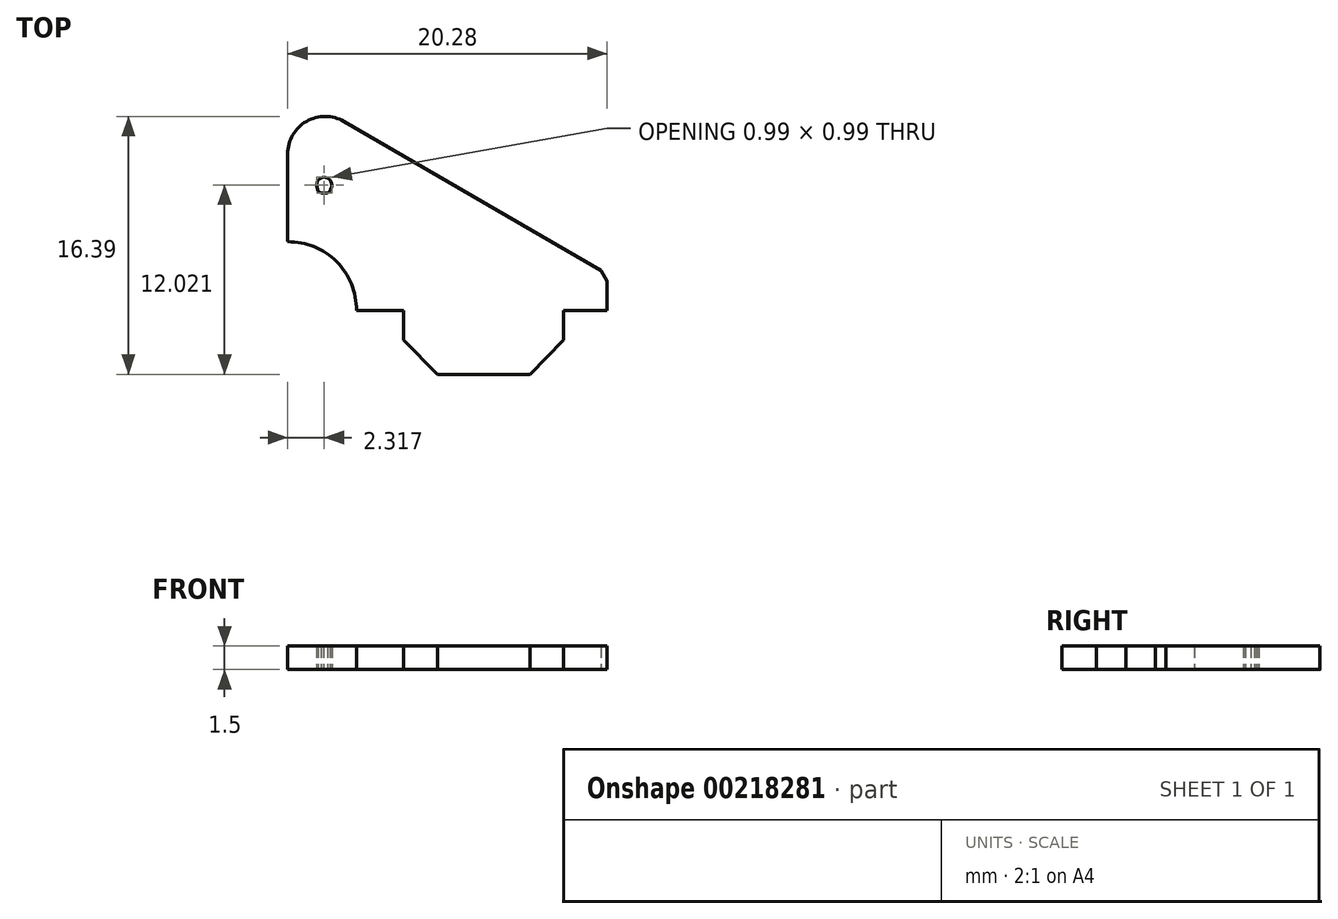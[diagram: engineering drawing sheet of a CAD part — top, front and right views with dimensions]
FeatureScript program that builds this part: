
annotation { "Feature Type Name" : "Feature", "Feature Type Description" : "" }
export const myFeature = defineFeature(function(context is Context, id is Id, definition is map)
    precondition{}
    {
        {
            var Q0;
            Q0=qCreatedBy(makeId("Top.planeOp"),FACE);
            var sketch = newSketch(context, id + "F0", { "sketchPlane" : qUnion([Q0])});
            skLineSegment(sketch, "E0", {"start": v(-0.76, -7.26) * mm, "end": v(5.12, -7.26) * mm});
            skLineSegment(sketch, "E1", {"start": v(5.12, -7.26) * mm, "end": v(7.23, -5.1) * mm});
            skLineSegment(sketch, "E2", {"start": v(7.23, -5.1) * mm, "end": v(7.23, -3.2) * mm});
            skLineSegment(sketch, "E3", {"start": v(7.23, -3.2) * mm, "end": v(10, -3.2) * mm});
            skLineSegment(sketch, "E4", {"start": v(10, -3.2) * mm, "end": v(10, -1.35) * mm});
            skLineSegment(sketch, "E5", {"start": v(-10.28, 1.16) * mm, "end": v(-10.28, 6.74) * mm});
            skLineSegment(sketch, "E6", {"start": v(-0.76, -7.26) * mm, "end": v(-2.94, -5.1) * mm});
            skLineSegment(sketch, "E7", {"start": v(-2.94, -5.1) * mm, "end": v(-2.94, -3.2) * mm});
            skLineSegment(sketch, "E8", {"start": v(-2.94, -3.2) * mm, "end": v(-5.92, -3.2) * mm});
            skLineSegment(sketch, "E9", {"start": v(-7.75, 4.26) * mm, "end": v(-7.58, 4.38) * mm});
            skLineSegment(sketch, "E10", {"start": v(-7.58, 4.38) * mm, "end": v(-7.47, 4.73) * mm});
            skLineSegment(sketch, "E11", {"start": v(-7.47, 4.73) * mm, "end": v(-7.52, 4.96) * mm});
            skLineSegment(sketch, "E12", {"start": v(-7.52, 4.96) * mm, "end": v(-7.58, 5.09) * mm});
            skLineSegment(sketch, "E13", {"start": v(-7.58, 5.09) * mm, "end": v(-7.75, 5.2) * mm});
            skLineSegment(sketch, "E14", {"start": v(-7.75, 5.2) * mm, "end": v(-8, 5.26) * mm});
            skLineSegment(sketch, "E15", {"start": v(-8, 5.26) * mm, "end": v(-8.16, 5.2) * mm});
            skLineSegment(sketch, "E16", {"start": v(-8.16, 5.2) * mm, "end": v(-8.34, 5.09) * mm});
            skLineSegment(sketch, "E17", {"start": v(-8.34, 5.09) * mm, "end": v(-8.4, 4.96) * mm});
            skLineSegment(sketch, "E18", {"start": v(-8.4, 4.96) * mm, "end": v(-8.46, 4.73) * mm});
            skLineSegment(sketch, "E19", {"start": v(-8.46, 4.73) * mm, "end": v(-8.34, 4.38) * mm});
            skLineSegment(sketch, "E20", {"start": v(-8.34, 4.38) * mm, "end": v(-8.16, 4.26) * mm});
            skLineSegment(sketch, "E21", {"start": v(-8.16, 4.26) * mm, "end": v(-7.75, 4.26) * mm});
            skLineSegment(sketch, "E22", {"start": v(-6.7, 8.8) * mm, "end": v(9.6, -0.66) * mm});
            skArc(sketch, "E23", {"start": v(-6.7, 8.8) * mm, "mid": v(-9.09, 8.8) * mm, "end": v(-10.28, 6.74) * mm});
            skArc(sketch, "E24", {"start": v(-5.92, -3.2) * mm, "mid": v(-7.17, -0.1) * mm, "end": v(-10.28, 1.16) * mm});
            skLineSegment(sketch, "E25", {"start": v(9.6, -0.66) * mm, "end": v(10, -1.35) * mm});
            skSolve(sketch);
        }
        {
            var Q0;
            Q0 = qSketchRegion(id + "F0", true);
            extrude(context, id + "F1", {"entities" : qUnion([Q0]), "depth" : 1.5 * mm});
        }
    });
